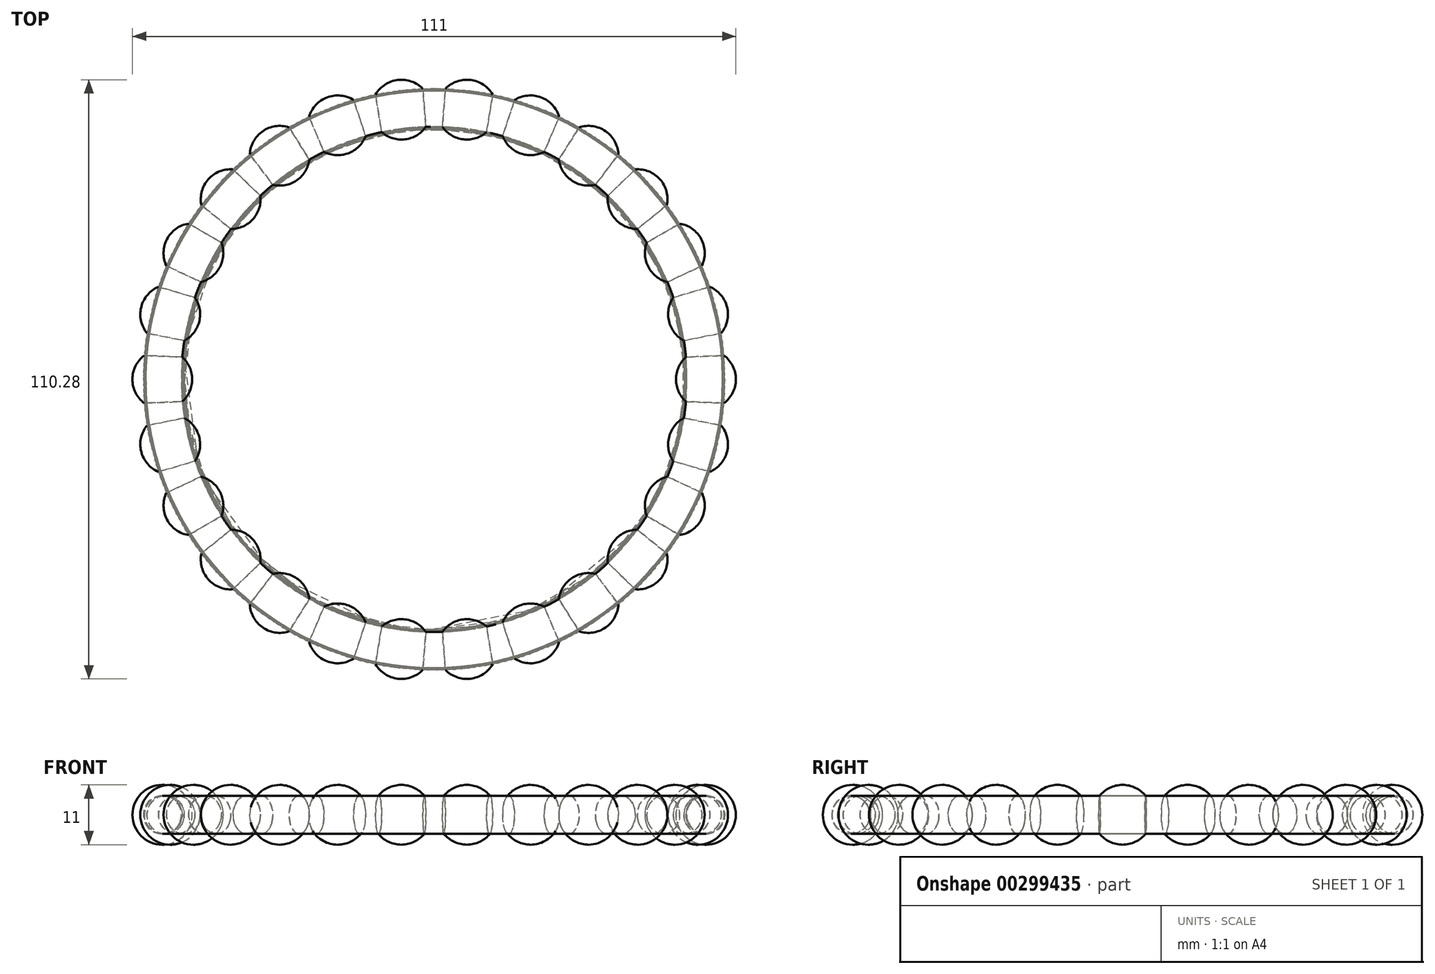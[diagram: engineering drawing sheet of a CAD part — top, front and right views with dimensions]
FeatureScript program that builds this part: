
annotation { "Feature Type Name" : "Feature", "Feature Type Description" : "" }
export const myFeature = defineFeature(function(context is Context, id is Id, definition is map)
    precondition{}
    {
        {
            var Q0;
            Q0=qCreatedBy(makeId("Front.planeOp"),FACE);
            var sketch = newSketch(context, id + "F0", { "sketchPlane" : qUnion([Q0])});
            skLineSegment(sketch, "E0", {"start": v(0, 26.2) * mm, "end": v(0, -23.35) * mm, "construction": true});
            skCircle(sketch, "E1", {"center": v(50, 0) * mm, "radius": 3.5 * mm});
            skSolve(sketch);
        }
        {
            var Q0;
            Q0=makeQuery(id+"F0.imprint","IMPRINT",FACE,{"disambiguationData":[TD([[makeQuery(id+"F0.imprint","IMPRINT",EDGE,{"derivedFrom":sQuery(id+"F0.wireOp",EDGE,"E1")}),1.0]])]});
            var Q1;
            Q1=sQuery(id+"F0.wireOp",EDGE,"E0");
            revolve(context, id + "F1", {"entities" : qUnion([Q0]), "axis" : qUnion([Q1]), "revolveType" : RevolveType.FULL});
        }
        {
            var Q0;
            Q0=qCreatedBy(makeId("Front.planeOp"),FACE);
            var sketch = newSketch(context, id + "F2", { "sketchPlane" : qUnion([Q0])});
            skLineSegment(sketch, "E2", {"start": v(-50, 3.5) * mm, "end": v(50, 3.5) * mm});
            skLineSegment(sketch, "E3", {"start": v(-50, -3.5) * mm, "end": v(50, -3.5) * mm});
            skArc(sketch, "E4", {"start": v(-50, -3.5) * mm, "mid": v(-46.5, 0) * mm, "end": v(-50, 3.5) * mm});
            skArc(sketch, "E5", {"start": v(50, 3.5) * mm, "mid": v(46.5, 0) * mm, "end": v(50, -3.5) * mm});
            skArc(sketch, "E6", {"start": v(50, -5.5) * mm, "mid": v(55.5, 0) * mm, "end": v(50, 5.5) * mm});
            skLineSegment(sketch, "E7", {"start": v(50, 5.5) * mm, "end": v(50, -5.5) * mm});
            skCircle(sketch, "E8", {"center": v(50, 0) * mm, "radius": 3.5 * mm});
            skSolve(sketch);
        }
        {
            var Q0;
            {var subQ0=sQuery(id+"F2.wireOp",EDGE,"E6");Q0=makeQuery(id+"F2.imprint","IMPRINT",FACE,{"disambiguationData":[TD([[makeQuery(id+"F2.imprint","IMPRINT",EDGE,{"derivedFrom":subQ0}),1.0]])]});}
            var Q1;
            Q1=sQuery(id+"F2.wireOp",EDGE,"E7");
            revolve(context, id + "F3", {"operationType" : NewBodyOperationType.ADD, "entities" : qUnion([Q0]), "axis" : qUnion([Q1]), "revolveType" : RevolveType.FULL});
        }
        {
            var Q0;
            Q0=makeQuery(id+"F1.opRevolve","SWEPT_BODY",BODY,{"disambiguationData":[OSD([sQuery(id+"F0.wireOp",EDGE,"E1")])]});
            var Q1;
            Q1=sQuery(id+"F0.wireOp",EDGE,"E0");
            circularPattern(context, id + "F4", {"entities" : qUnion([Q0]), "axis" : qUnion([Q1]), "angle" : 360 * degree, "instanceCount" : 26, "equalSpace" : true});
        }
        {
            var Q0;
            Q0=qCreatedBy(makeId("Front.planeOp"),FACE);
            var sketch = newSketch(context, id + "F5", { "sketchPlane" : qUnion([Q0])});
            skLineSegment(sketch, "E9", {"start": v(50, 7.5) * mm, "end": v(50, -7.5) * mm});
            skSolve(sketch);
        }
        {
            var Q0;
            Q0=qCreatedBy(makeId("Top.planeOp"),FACE);
            var sketch = newSketch(context, id + "F6", { "sketchPlane" : qUnion([Q0])});
            skCircle(sketch, "E10", {"center": v(0, 0) * mm, "radius": 50 * mm});
            skSolve(sketch);
        }
    });
